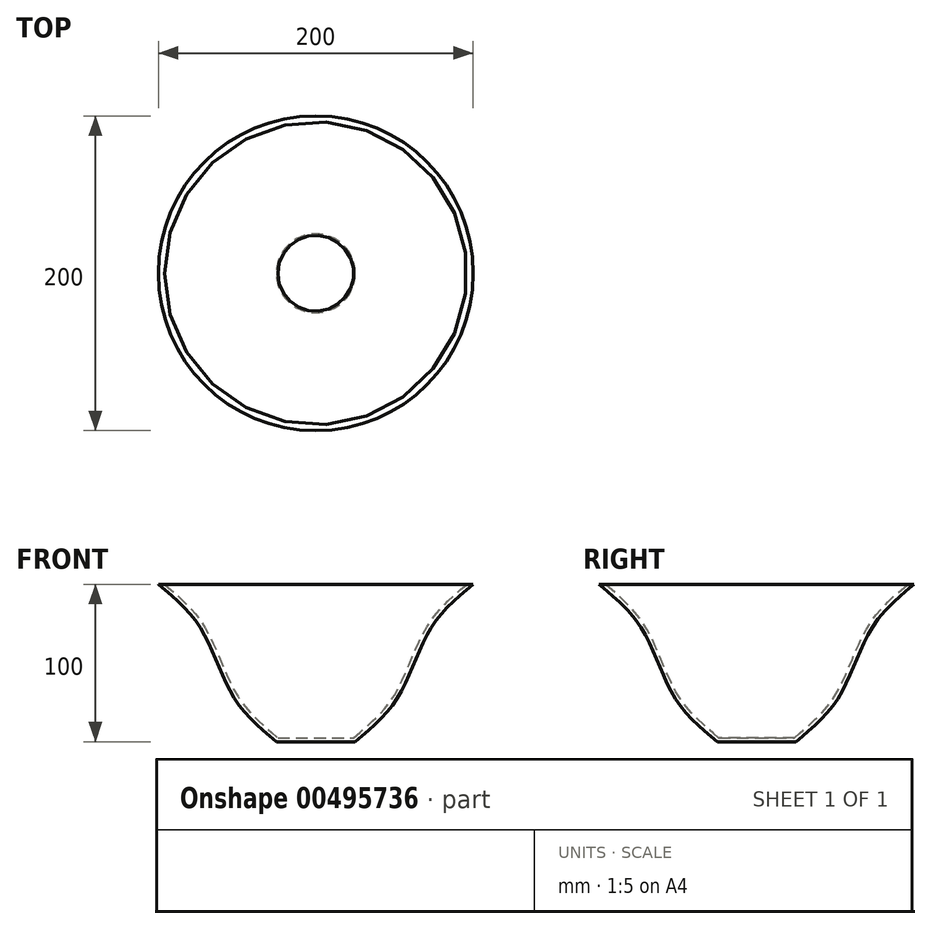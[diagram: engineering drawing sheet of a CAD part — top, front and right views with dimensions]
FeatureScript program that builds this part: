
annotation { "Feature Type Name" : "Feature", "Feature Type Description" : "" }
export const myFeature = defineFeature(function(context is Context, id is Id, definition is map)
    precondition{}
    {
        {
            var Q0;
            Q0=qCreatedBy(makeId("Top.planeOp"),FACE);
            cPlane(context, id + "F0", {"entities" : qUnion([Q0]), "cplaneType" : CPlaneType.OFFSET, "offset" : 25 * mm, "width" : 150 * mm, "height" : 150 * mm});
        }
        {
            var Q0;
            Q0=qCreatedBy(id+"F0.planeOp",FACE);
            cPlane(context, id + "F1", {"entities" : qUnion([Q0]), "cplaneType" : CPlaneType.OFFSET, "offset" : 25 * mm, "width" : 150 * mm, "height" : 150 * mm});
        }
        {
            var Q0;
            Q0=qCreatedBy(id+"F1.planeOp",FACE);
            cPlane(context, id + "F2", {"entities" : qUnion([Q0]), "cplaneType" : CPlaneType.OFFSET, "offset" : 25 * mm, "width" : 150 * mm, "height" : 150 * mm});
        }
        {
            var Q0;
            Q0=qCreatedBy(id+"F2.planeOp",FACE);
            cPlane(context, id + "F3", {"entities" : qUnion([Q0]), "cplaneType" : CPlaneType.OFFSET, "offset" : 25 * mm, "width" : 150 * mm, "height" : 150 * mm});
        }
        {
            var Q0;
            Q0=qCreatedBy(id+"F3.planeOp",FACE);
            var sketch = newSketch(context, id + "F4", { "sketchPlane" : qUnion([Q0])});
            skCircle(sketch, "E0", {"center": v(0, 0) * mm, "radius": 100 * mm});
            skSolve(sketch);
        }
        {
            var Q0;
            Q0=qCreatedBy(id+"F2.planeOp",FACE);
            var sketch = newSketch(context, id + "F5", { "sketchPlane" : qUnion([Q0])});
            skCircle(sketch, "E1", {"center": v(0, 0) * mm, "radius": 75 * mm});
            skSolve(sketch);
        }
        {
            var Q0;
            Q0=qCreatedBy(id+"F1.planeOp",FACE);
            var sketch = newSketch(context, id + "F6", { "sketchPlane" : qUnion([Q0])});
            skCircle(sketch, "E2", {"center": v(0, 0) * mm, "radius": 62.5 * mm});
            skSolve(sketch);
        }
        {
            var Q0;
            Q0=qCreatedBy(id+"F0.planeOp",FACE);
            var sketch = newSketch(context, id + "F7", { "sketchPlane" : qUnion([Q0])});
            skCircle(sketch, "E3", {"center": v(0, 0) * mm, "radius": 50 * mm});
            skSolve(sketch);
        }
        {
            var Q0;
            Q0=qCreatedBy(makeId("Top.planeOp"),FACE);
            var sketch = newSketch(context, id + "F8", { "sketchPlane" : qUnion([Q0])});
            skCircle(sketch, "E4", {"center": v(0, 0) * mm, "radius": 25 * mm});
            skSolve(sketch);
        }
        {
            var Q0;
            Q0=makeQuery(id+"F4.imprint","IMPRINT",FACE,{"disambiguationData":[TD([[makeQuery(id+"F4.imprint","IMPRINT",EDGE,{"derivedFrom":sQuery(id+"F4.wireOp",EDGE,"E0")}),1.0]])]});
            var Q1;
            Q1=makeQuery(id+"F5.imprint","IMPRINT",FACE,{"disambiguationData":[TD([[makeQuery(id+"F5.imprint","IMPRINT",EDGE,{"derivedFrom":sQuery(id+"F5.wireOp",EDGE,"E1")}),1.0]])]});
            var Q2;
            Q2=makeQuery(id+"F6.imprint","IMPRINT",FACE,{"disambiguationData":[TD([[makeQuery(id+"F6.imprint","IMPRINT",EDGE,{"derivedFrom":sQuery(id+"F6.wireOp",EDGE,"E2")}),1.0]])]});
            var Q3;
            Q3=makeQuery(id+"F7.imprint","IMPRINT",FACE,{"disambiguationData":[TD([[makeQuery(id+"F7.imprint","IMPRINT",EDGE,{"derivedFrom":sQuery(id+"F7.wireOp",EDGE,"E3")}),1.0]])]});
            var Q4;
            Q4=makeQuery(id+"F8.imprint","IMPRINT",FACE,{"disambiguationData":[TD([[makeQuery(id+"F8.imprint","IMPRINT",EDGE,{"derivedFrom":sQuery(id+"F8.wireOp",EDGE,"E4")}),1.0]])]});
            loft(context, id + "F9", {"sheetProfilesArray" : [{ "sheetProfileEntities" : qUnion([Q0]) }, { "sheetProfileEntities" : qUnion([Q1]) }, { "sheetProfileEntities" : qUnion([Q2]) }, { "sheetProfileEntities" : qUnion([Q3]) }, { "sheetProfileEntities" : qUnion([Q4]) }]});
        }
        {
            var Q0;
            Q0=makeQuery(id+"F9.opLoft","CAP_FACE",FACE,{"disambiguationData":[OSD([makeQuery(id+"F4.imprint","IMPRINT",FACE,{"disambiguationData":[TD([[makeQuery(id+"F4.imprint","IMPRINT",EDGE,{"derivedFrom":sQuery(id+"F4.wireOp",EDGE,"E0")}),1.0]])]})])],"isStart":true});
            shell(context, id + "F10", {"entities" : qUnion([Q0]), "thickness" : 2.5 * mm});
        }
    });
